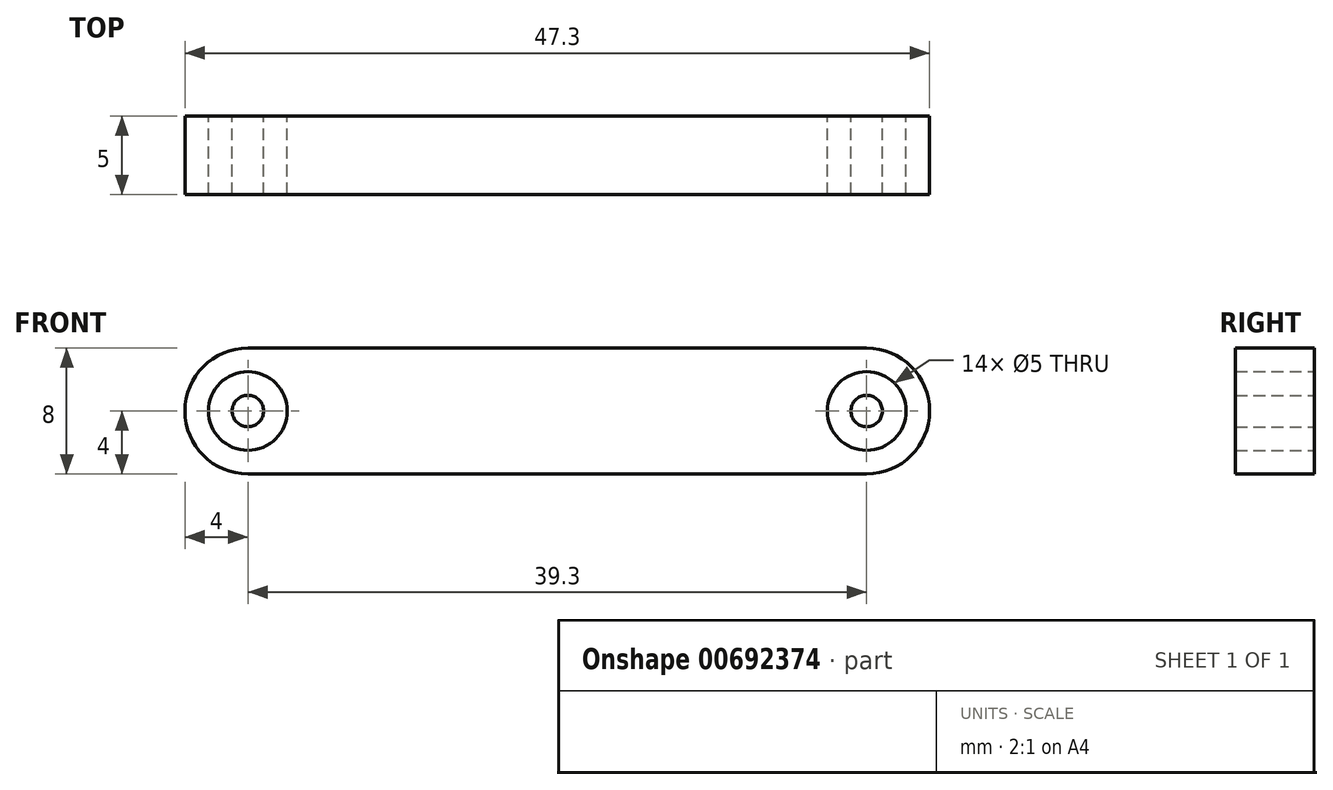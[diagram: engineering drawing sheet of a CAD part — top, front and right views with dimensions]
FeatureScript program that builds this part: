
annotation { "Feature Type Name" : "Feature", "Feature Type Description" : "" }
export const myFeature = defineFeature(function(context is Context, id is Id, definition is map)
    precondition{}
    {
        {
            var Q0;
            Q0=qCreatedBy(makeId("Front.planeOp"),FACE);
            var sketch = newSketch(context, id + "F0", { "sketchPlane" : qUnion([Q0])});
            skArc(sketch, "E0", {"start": v(0, 4) * mm, "mid": v(-4, 0) * mm, "end": v(0, -4) * mm});
            skArc(sketch, "E1", {"start": v(39.3, -4) * mm, "mid": v(43.3, 0) * mm, "end": v(39.3, 4) * mm});
            skLineSegment(sketch, "E2", {"start": v(0, 4) * mm, "end": v(39.3, 4) * mm});
            skLineSegment(sketch, "E3", {"start": v(0, -4) * mm, "end": v(39.3, -4) * mm});
            skCircle(sketch, "E4", {"center": v(0, 0) * mm, "radius": 2.5 * mm});
            skCircle(sketch, "E5", {"center": v(39.3, 0) * mm, "radius": 2.5 * mm});
            skCircle(sketch, "E6", {"center": v(39.3, 0) * mm, "radius": 1 * mm});
            skCircle(sketch, "E7", {"center": v(0, 0) * mm, "radius": 1 * mm});
            skSolve(sketch);
        }
        {
            var Q0;
            Q0 = qSketchRegion(id + "F0", true);
            var Q1;
            Q1=makeQuery(id+"F0.imprint","IMPRINT",FACE,{"disambiguationData":[TD([[makeQuery(id+"F0.imprint","IMPRINT",EDGE,{"derivedFrom":sQuery(id+"F0.wireOp",EDGE,"E7")}),1.0]])]});
            var Q2;
            Q2=makeQuery(id+"F0.imprint","IMPRINT",FACE,{"disambiguationData":[TD([[makeQuery(id+"F0.imprint","IMPRINT",EDGE,{"derivedFrom":sQuery(id+"F0.wireOp",EDGE,"E6")}),1.0]])]});
            extrude(context, id + "F1", {"entities" : qUnion([Q0, Q1, Q2]), "depth" : 5 * mm, "offsetDistance" : 25 * mm});
        }
    });
